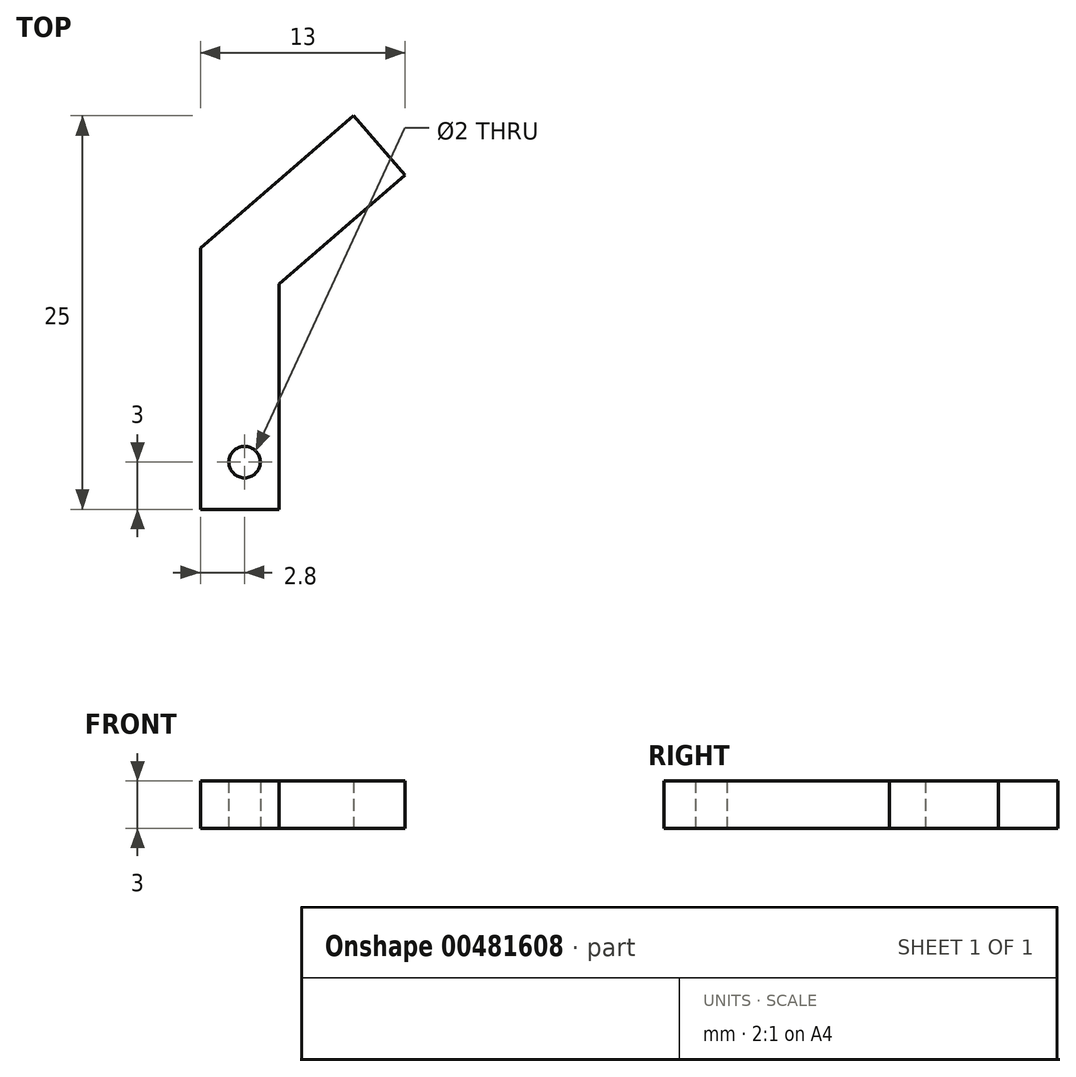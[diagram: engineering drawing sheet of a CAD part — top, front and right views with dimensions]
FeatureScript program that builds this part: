
annotation { "Feature Type Name" : "Feature", "Feature Type Description" : "" }
export const myFeature = defineFeature(function(context is Context, id is Id, definition is map)
    precondition{}
    {
        {
            var Q0;
            Q0=qCreatedBy(makeId("Top.planeOp"),FACE);
            var sketch = newSketch(context, id + "F0", { "sketchPlane" : qUnion([Q0])});
            skLineSegment(sketch, "E0", {"start": v(-2.8, 0) * mm, "end": v(-2.8, 16.6) * mm});
            skLineSegment(sketch, "E1", {"start": v(-2.8, 16.6) * mm, "end": v(6.93, 25) * mm});
            skLineSegment(sketch, "E2", {"start": v(6.93, 25) * mm, "end": v(10.2, 21.22) * mm});
            skLineSegment(sketch, "E3", {"start": v(10.2, 21.22) * mm, "end": v(2.2, 14.3) * mm});
            skLineSegment(sketch, "E4", {"start": v(2.2, 14.3) * mm, "end": v(2.2, 0) * mm});
            skLineSegment(sketch, "E5", {"start": v(2.2, 0) * mm, "end": v(-2.8, 0) * mm});
            skCircle(sketch, "E6", {"center": v(0, 3) * mm, "radius": 1 * mm});
            skSolve(sketch);
        }
        {
            var Q0;
            Q0 = qSketchRegion(id + "F0", true);
            extrude(context, id + "F1", {"entities" : qUnion([Q0]), "depth" : 3 * mm});
        }
    });
